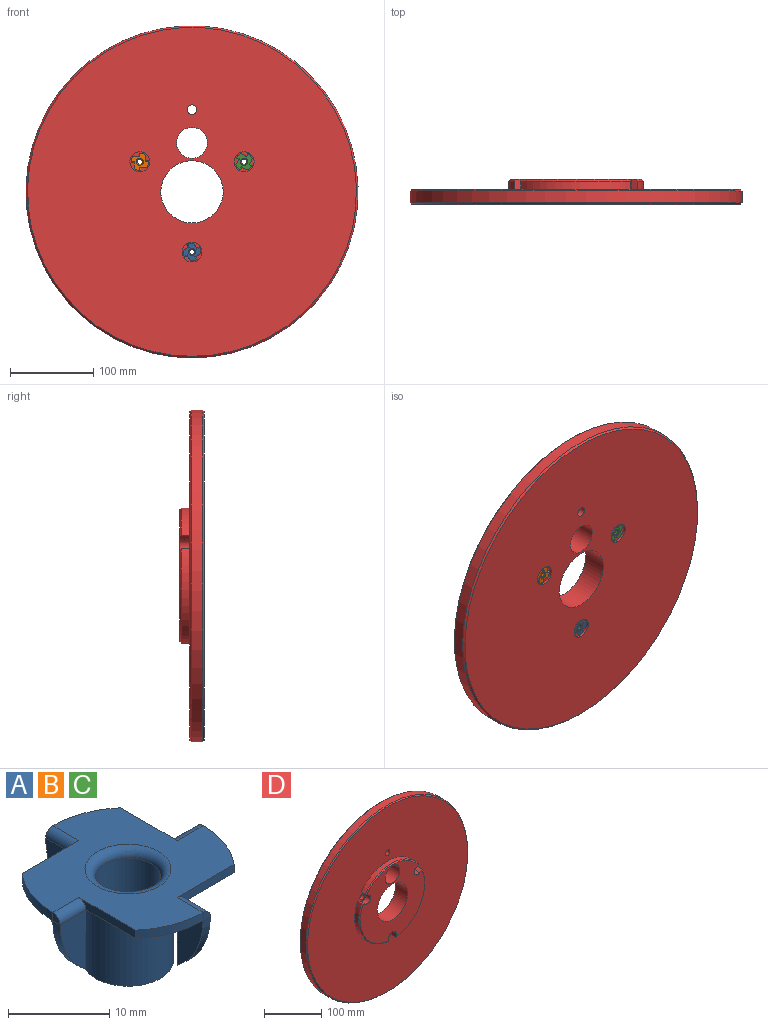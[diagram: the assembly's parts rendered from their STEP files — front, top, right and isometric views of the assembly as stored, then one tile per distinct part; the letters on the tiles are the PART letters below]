
ASSEMBLY  parts=4 mates=1
PART A: 39 faces, bbox 21x21x11 mm
  f0: cylinder r=10.5mm len=6.88mm, axis (0,0,-1), area 7.5mm2, adj f1,f2,f6,f34
  f1: plane 21x21mm, normal (0,0,1), area 209.8mm2, adj f0,f6,f7,f8,f9,f10,f11,f12
  f2: plane 21x20.99mm, normal (0,0,-1), area 201.1mm2, adj f0,f4,f6,f7,f8,f9,f10,f11
  f3: cylinder r=3.25mm len=10mm, axis (0,0,-1), area 204.2mm2, adj f5,f38
  f4: cylinder r=4.5mm len=10mm, axis (0,0,1), area 282.7mm2, adj f2,f5
  f5: plane 9x9mm, normal (0,0,-1), area 30.4mm2, adj f3,f4
  f6: plane 7.94x1mm, normal (1,0,0), area 7.2mm2, adj f0,f1,f2,f31
  f7: cylinder r=10.5mm len=6.88mm, axis (0,0,-1), area 7.5mm2, adj f1,f2,f8,f15,f16,f19
  f8: plane 7.94x1mm, normal (0,1,0), area 7.2mm2, adj f1,f2,f7,f37
  f9: cylinder r=10.5mm len=6.88mm, axis (0,0,-1), area 7.5mm2, adj f1,f2,f10,f22
  f10: plane 7.94x1mm, normal (-1,0,0), area 7.2mm2, adj f1,f2,f9,f18
  f11: cylinder r=10.5mm len=6.88mm, axis (0,0,-1), area 7.5mm2, adj f1,f2,f12,f28
  f12: plane 7.94x1mm, normal (0,-1,0), area 7.2mm2, adj f1,f2,f11,f25
  f13: plane 7.2x1.5mm, normal (1,0,0), area 7.3mm2, adj f2,f14,f16,f17,f19
  f14: plane 6.7x3.61mm, normal (0,1,0), area 16.4mm2, adj f13,f16,f19
  f15: plane 1x1mm, normal (-1,0,0), area 0.8mm2, adj f7,f16,f18
  f16: cylinder r=8.96mm len=7.2mm, axis (0,1,0), area 8.4mm2, adj f7,f13,f14,f15,f17,f19
  f17: plane 7.2x3.63mm, normal (0,-1,0), area 18.3mm2, adj f13,f16,f18
  f18: cylinder r=1mm len=3.63mm, axis (-1,0,0), area 5.7mm2, adj f1,f10,f15,f17
  f19: cylinder r=0.5mm len=3.62mm, axis (1,0,0), area 2.8mm2, adj f2,f7,f13,f14,f16
  f20: plane 7.2x1mm, normal (0,1,0), area 7.2mm2, adj f2,f21,f23,f24
  f21: plane 7.2x3.63mm, normal (-1,0,0), area 18.3mm2, adj f2,f20,f23
  f22: plane 1x1mm, normal (0,-1,0), area 0.8mm2, adj f9,f23,f25
  f23: cylinder r=8.96mm len=7.2mm, axis (-1,0,0), area 8.4mm2, adj f20,f21,f22,f24
  f24: plane 7.2x3.63mm, normal (1,0,0), area 18.3mm2, adj f20,f23,f25
  f25: cylinder r=1mm len=3.63mm, axis (0,-1,0), area 5.7mm2, adj f1,f12,f22,f24
  f26: plane 7.2x1mm, normal (-1,0,0), area 7.2mm2, adj f2,f27,f29,f30
  f27: plane 7.2x3.63mm, normal (0,-1,0), area 18.3mm2, adj f2,f26,f29
  f28: plane 1x1mm, normal (1,0,0), area 0.8mm2, adj f11,f29,f31
  f29: cylinder r=8.96mm len=7.2mm, axis (0,-1,0), area 8.4mm2, adj f26,f27,f28,f30
  f30: plane 7.2x3.63mm, normal (0,1,0), area 18.3mm2, adj f26,f29,f31
  f31: cylinder r=1mm len=3.63mm, axis (1,0,0), area 5.7mm2, adj f1,f6,f28,f30
  f32: plane 7.2x1mm, normal (0,-1,0), area 7.2mm2, adj f2,f33,f35,f36
  f33: plane 7.2x3.63mm, normal (1,0,0), area 18.3mm2, adj f2,f32,f35
  f34: plane 1x1mm, normal (0,1,0), area 0.8mm2, adj f0,f35,f37
  f35: cylinder r=8.96mm len=7.2mm, axis (1,0,0), area 8.4mm2, adj f32,f33,f34,f36
  f36: plane 7.2x3.63mm, normal (-1,0,0), area 18.3mm2, adj f32,f35,f37
  f37: cylinder r=1mm len=3.63mm, axis (0,1,0), area 5.7mm2, adj f1,f8,f34,f36
  f38: torus R=4.25mm, axis (0,0,1), area 35.7mm2, adj f1,f3
PART B: same geometry as A
PART C: same geometry as A
PART D: 33 faces, bbox 400x30x400 mm
  f0: cylinder r=81.5mm len=113.71mm, axis (0,1,0), area 1526.6mm2, adj f10,f19,f27,f32
  f1: cylinder r=5.75mm len=15mm, axis (0,1,0), area 541.9mm2, adj f10,f13
  f2: cylinder r=81.5mm len=113.71mm, axis (0,1,0), area 1526.6mm2, adj f10,f24,f25,f30
  f3: cylinder r=5.75mm len=15mm, axis (0,1,0), area 541.9mm2, adj f10,f17
  f4: cylinder r=81.5mm len=131.3mm, axis (0,1,0), area 1526.6mm2, adj f10,f21,f22,f31
  f5: cylinder r=5.75mm len=15mm, axis (0,1,0), area 541.9mm2, adj f10,f15
  f6: cylinder r=37.5mm len=75mm, axis (0,1,0), area 7068.6mm2, adj f11,f12
  f7: cylinder r=18.5mm len=37mm, axis (0,1,0), area 3487.2mm2, adj f11,f12
  f8: cylinder r=5.75mm len=18mm, axis (0,1,0), area 650.3mm2, adj f10,f11
  f9: cylinder r=200mm len=400mm, axis (0,1,0), area 17592.9mm2, adj f28,f29
  f10: plane 396x396mm, normal (0,-1,0), area 102739mm2, adj f0,f1,f2,f3,f4,f5,f8,f19
  f11: plane 396x396mm, normal (0,1,0), area 116208.9mm2, adj f6,f7,f8,f14,f16,f18,f28
  f12: plane 159x158.49mm, normal (0,-1,0), area 13612.1mm2, adj f6,f7,f19,f20,f21,f22,f23,f24
  f13: plane 24x24mm, normal (0,1,0), area 348.5mm2, adj f1,f14
  f14: cylinder r=12mm len=24mm, axis (0,1,0), area 226.2mm2, adj f11,f13
  f15: plane 24x24mm, normal (0,1,0), area 348.5mm2, adj f5,f16
  f16: cylinder r=12mm len=24mm, axis (0,1,0), area 226.2mm2, adj f11,f15
  f17: plane 24x24mm, normal (0,1,0), area 348.5mm2, adj f3,f18
  f18: cylinder r=12mm len=24mm, axis (0,1,0), area 226.2mm2, adj f11,f17
  f19: plane 12x7.37mm, normal (-0.5,0,0.87), area 100mm2, adj f0,f10,f12,f20,f32
  f20: cylinder r=9mm len=16.79mm, axis (0,-1,0), area 339.3mm2, adj f10,f12,f19,f21
  f21: plane 12x7.37mm, normal (0.5,0,-0.87), area 100mm2, adj f4,f10,f12,f20,f31
  f22: plane 12x7.37mm, normal (-0.5,0,-0.87), area 100mm2, adj f4,f10,f12,f23,f31
  f23: cylinder r=9mm len=16.79mm, axis (0,-1,0), area 339.3mm2, adj f10,f12,f22,f24
  f24: plane 12x7.37mm, normal (0.5,0,0.87), area 100mm2, adj f2,f10,f12,f23,f30
  f25: plane 12x8.5mm, normal (1,0,0), area 100mm2, adj f2,f10,f12,f26,f30
  f26: cylinder r=9mm len=18mm, axis (0,-1,0), area 339.3mm2, adj f10,f12,f25,f27
  f27: plane 12x8.5mm, normal (-1,0,0), area 100mm2, adj f0,f10,f12,f26,f32
  f28: cone r=200mm half-angle=45deg, axis (0,-1,0), area 3536.5mm2, adj f9,f11
  f29: cone r=198mm half-angle=45deg, axis (0,1,0), area 3536.5mm2, adj f9,f10
  f30: cone r=79.5mm half-angle=45deg, axis (0,1,0), area 425.8mm2, adj f2,f12,f24,f25
  f31: cone r=79.5mm half-angle=45deg, axis (0,1,0), area 425.8mm2, adj f4,f12,f21,f22
  f32: cone r=79.5mm half-angle=45deg, axis (0,1,0), area 425.8mm2, adj f0,f12,f19,f27
PLACE A rot(axis=(0.77,0.45,-0.45),104.5deg) t=(-25.76,42.54,-53.47)mm
PLACE B rot(axis=(0,-0.71,0.71),180deg) t=(-88.55,42.54,55.28)mm
PLACE C rot(axis=(0.77,-0.45,0.45),104.5deg) t=(37.03,42.54,55.28)mm
PLACE D rot(axis=(0,0,1),180deg) t=(-25.76,39.54,19.03)mm
MATE fastened B.f4 <-> D.f5  axis (0,1,0) through (-88.55,52.54,55.28)mm
